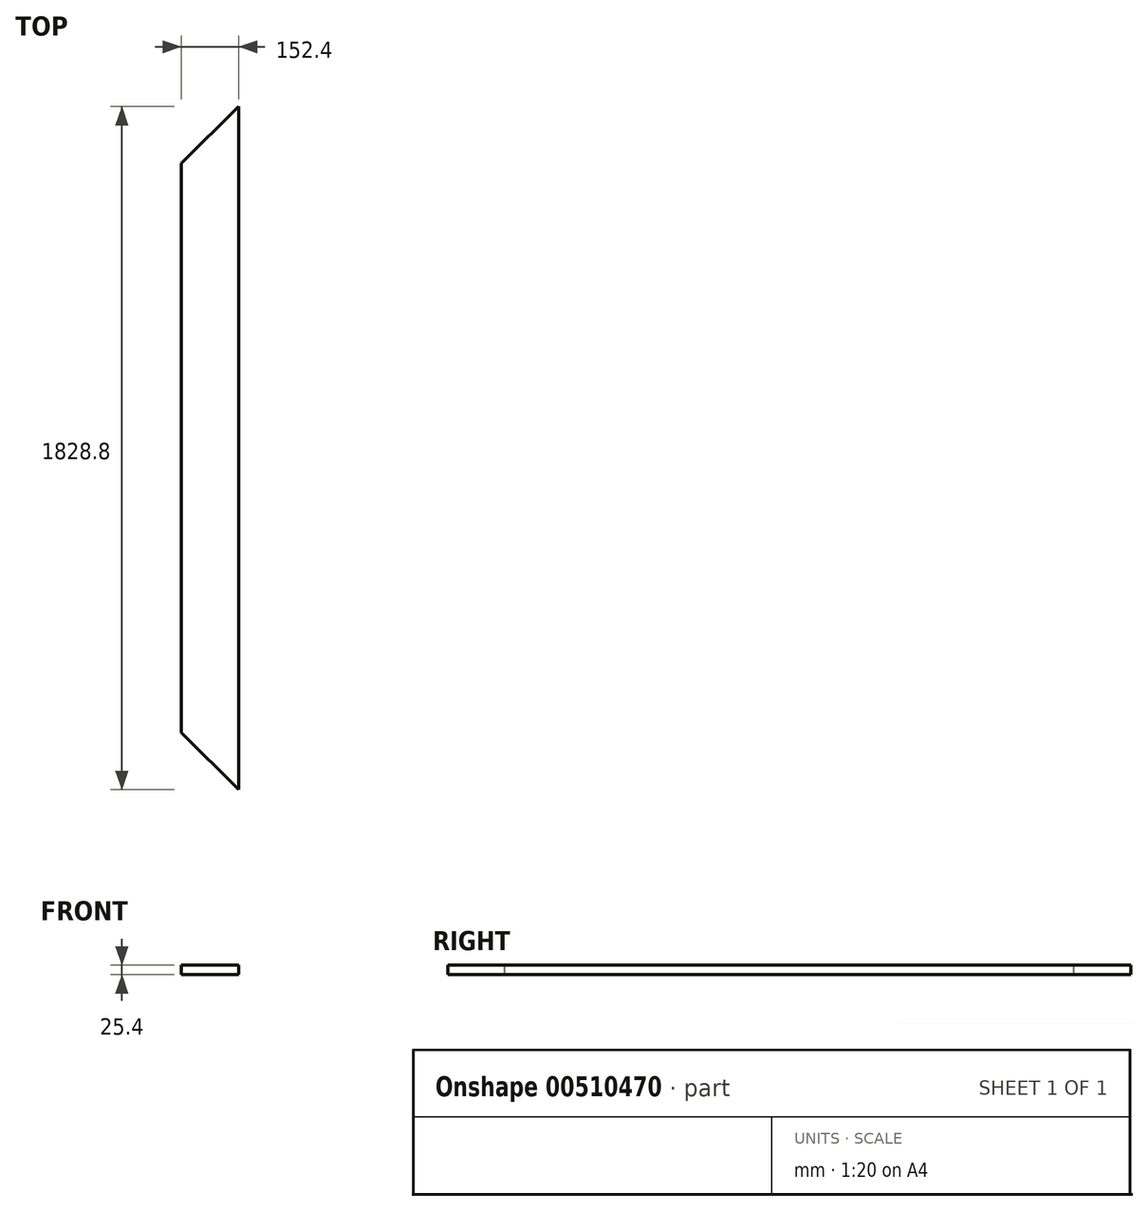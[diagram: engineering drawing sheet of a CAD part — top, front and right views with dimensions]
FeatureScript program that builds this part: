
annotation { "Feature Type Name" : "Feature", "Feature Type Description" : "" }
export const myFeature = defineFeature(function(context is Context, id is Id, definition is map)
    precondition{}
    {
        {
            var Q0;
            Q0=qCreatedBy(makeId("Front.planeOp"),FACE);
            var sketch = newSketch(context, id + "F0", { "sketchPlane" : qUnion([Q0])});
            skLineSegment(sketch, "E0.bottom", {"start": v(-70.87, 30.93) * mm, "end": v(81.53, 30.93) * mm});
            skLineSegment(sketch, "E0.top", {"start": v(-70.87, 5.53) * mm, "end": v(81.53, 5.53) * mm});
            skLineSegment(sketch, "E0.left", {"start": v(-70.87, 30.93) * mm, "end": v(-70.87, 5.53) * mm});
            skLineSegment(sketch, "E0.right", {"start": v(81.53, 30.93) * mm, "end": v(81.53, 5.53) * mm});
            skSolve(sketch);
        }
        {
            var Q0;
            Q0=makeQuery(id+"F0.imprint","IMPRINT",FACE,{"disambiguationData":[TD([[makeQuery(id+"F0.imprint","IMPRINT",EDGE,{"derivedFrom":sQuery(id+"F0.wireOp",EDGE,"E0.bottom")}),-1.0]])]});
            extrude(context, id + "F1", {"entities" : qUnion([Q0]), "depth" : 1828.8 * mm});
        }
        {
            var Q0;
            Q0=makeQuery(id+"F1.opExtrude","SWEPT_FACE",FACE,{"disambiguationData":[OSD([sQuery(id+"F0.wireOp",EDGE,"E0.bottom")])]});
            var sketch = newSketch(context, id + "F2", { "sketchPlane" : qUnion([Q0])});
            skLineSegment(sketch, "E1", {"start": v(81.53, 0) * mm, "end": v(-70.87, -152.4) * mm});
            skLineSegment(sketch, "E2", {"start": v(81.53, -1828.8) * mm, "end": v(-70.87, -1676.4) * mm});
            skSolve(sketch);
        }
        {
            var Q0;
            {var subQ0=sQuery(id+"F2.wireOp",EDGE,"E1");Q0=makeQuery(id+"F2.imprint","IMPRINT",FACE,{"disambiguationData":[TD([[makeQuery(id+"F2.imprint","IMPRINT",EDGE,{"derivedFrom":subQ0}),-1.0]])]});}
            var Q1;
            {var subQ0=sQuery(id+"F2.wireOp",EDGE,"E2");Q1=makeQuery(id+"F2.imprint","IMPRINT",FACE,{"disambiguationData":[TD([[makeQuery(id+"F2.imprint","IMPRINT",EDGE,{"derivedFrom":subQ0}),1.0]])]});}
            extrude(context, id + "F3", {"entities" : qUnion([Q0, Q1]), "operationType" : NewBodyOperationType.REMOVE, "oppositeDirection" : true, "depth" : 182.88 * mm});
        }
    });
